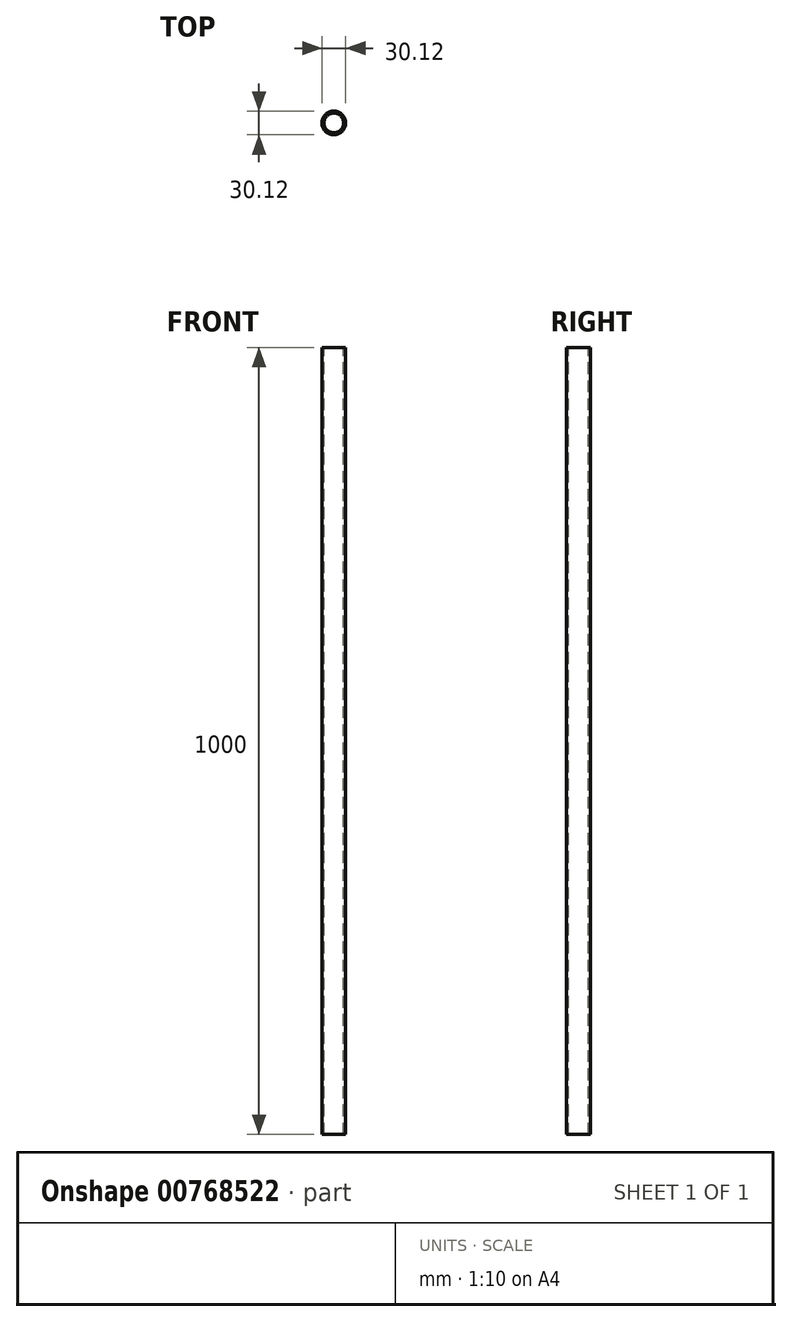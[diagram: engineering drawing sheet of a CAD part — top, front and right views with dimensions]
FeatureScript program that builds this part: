
annotation { "Feature Type Name" : "Feature", "Feature Type Description" : "" }
export const myFeature = defineFeature(function(context is Context, id is Id, definition is map)
    precondition{}
    {
        {
            var Q0;
            Q0=qCreatedBy(makeId("Top.planeOp"),FACE);
            var sketch = newSketch(context, id + "F0", { "sketchPlane" : qUnion([Q0])});
            skCircle(sketch, "E0", {"center": v(0, 0) * mm, "radius": 12.5 * mm});
            skSolve(sketch);
        }
        {
            var Q0;
            Q0=qCreatedBy(makeId("Top.planeOp"),FACE);
            var sketch = newSketch(context, id + "F1", { "sketchPlane" : qUnion([Q0])});
            skCircle(sketch, "E1", {"center": v(0, 0) * mm, "radius": 15.06 * mm});
            skSolve(sketch);
        }
        {
            var Q0;
            Q0=sQuery(id+"F1.wireOp",EDGE,"E1");
            var Q1;
            Q1=sQuery(id+"F0.wireOp",EDGE,"E0");
            extrude(context, id + "F2", {"bodyType" : ToolBodyType.SURFACE, "surfaceEntities" : qUnion([Q0, Q1]), "depth" : 1000 * mm, "offsetDistance" : 25 * mm});
        }
    });
